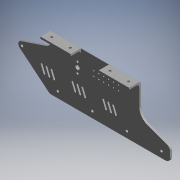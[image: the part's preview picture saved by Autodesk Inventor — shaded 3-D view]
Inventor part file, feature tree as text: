
AUTODESK INVENTOR PART (.ipt)
format: ipt  version: 2019 (Build 230136000, 136)  size: 275,456 bytes
history: native  units: mm (DEFAULTED — no unit token found)
features: extrude x3, fillet x3, sketch x3
ambient origin geometry x8: Origin, YZ Plane, XZ Plane, XY Plane, X Axis, Y Axis, Z Axis, Center Point
bodies: Body1 (feature_tree)
feature tree (9):
  extrude  "Extrusion4"  Depth=22.0mm
  extrude  "Extrusion5"  Depth=50.0mm
  extrude  "Extrusion6"  Depth=4.5mm
  fillet  "Fillet1"  Radius=40.0mm
  fillet  "Fillet2"  Radius=44.7mm
  fillet  "Fillet3"  Radius=190.0mm
  sketch  "Sketch1"  dims[d0=195.0mm d1=22.0mm]
  sketch  "Sketch2"  dims[d2=89.0mm d3=50.0mm]
  sketch  "Sketch3"  dims[d5=143.5mm d6=22.5mm d7=40.0mm d11=44.7mm d12=190.0mm d13=6.0mm d14=7.0mm d15=20.0mm d16=10.0mm d19=4.0mm d20=4.0mm d21=4.0mm d22=4.0mm d23=168.0mm d24=56.0mm d25=56.0mm d26=56.0mm d27=10.0mm d28=14.0mm d29=4.0mm d32=7.0mm d33=59.2mm d34=100.0mm d35=3.5mm d36=3.5mm d37=16.5mm d40=3.0mm d41=3.0mm d42=12.0mm d43=30.0mm d45=8.0mm d46=10.0mm d48=10.0mm d50=30.0mm d52=50.0mm d53=10.0mm d55=10.0mm d57=2.0mm d58=20.0mm d60=8.0mm d61=60.0mm d63=8.0mm d66=3.0mm d67=0.0mm d68=49.0mm d69=3.0mm d70=49.0mm d71=3.0mm d72=16.5mm d73=0.0mm d74=4.0mm d75=4.0mm d76=16.5mm d77=8.25mm d78=4.0mm d79=4.0mm d80=30.0mm d81=30.0mm d82=16.5mm d83=0.0mm d84=4.5mm d85=4.5mm d86=4.5mm d87=25.0mm]
